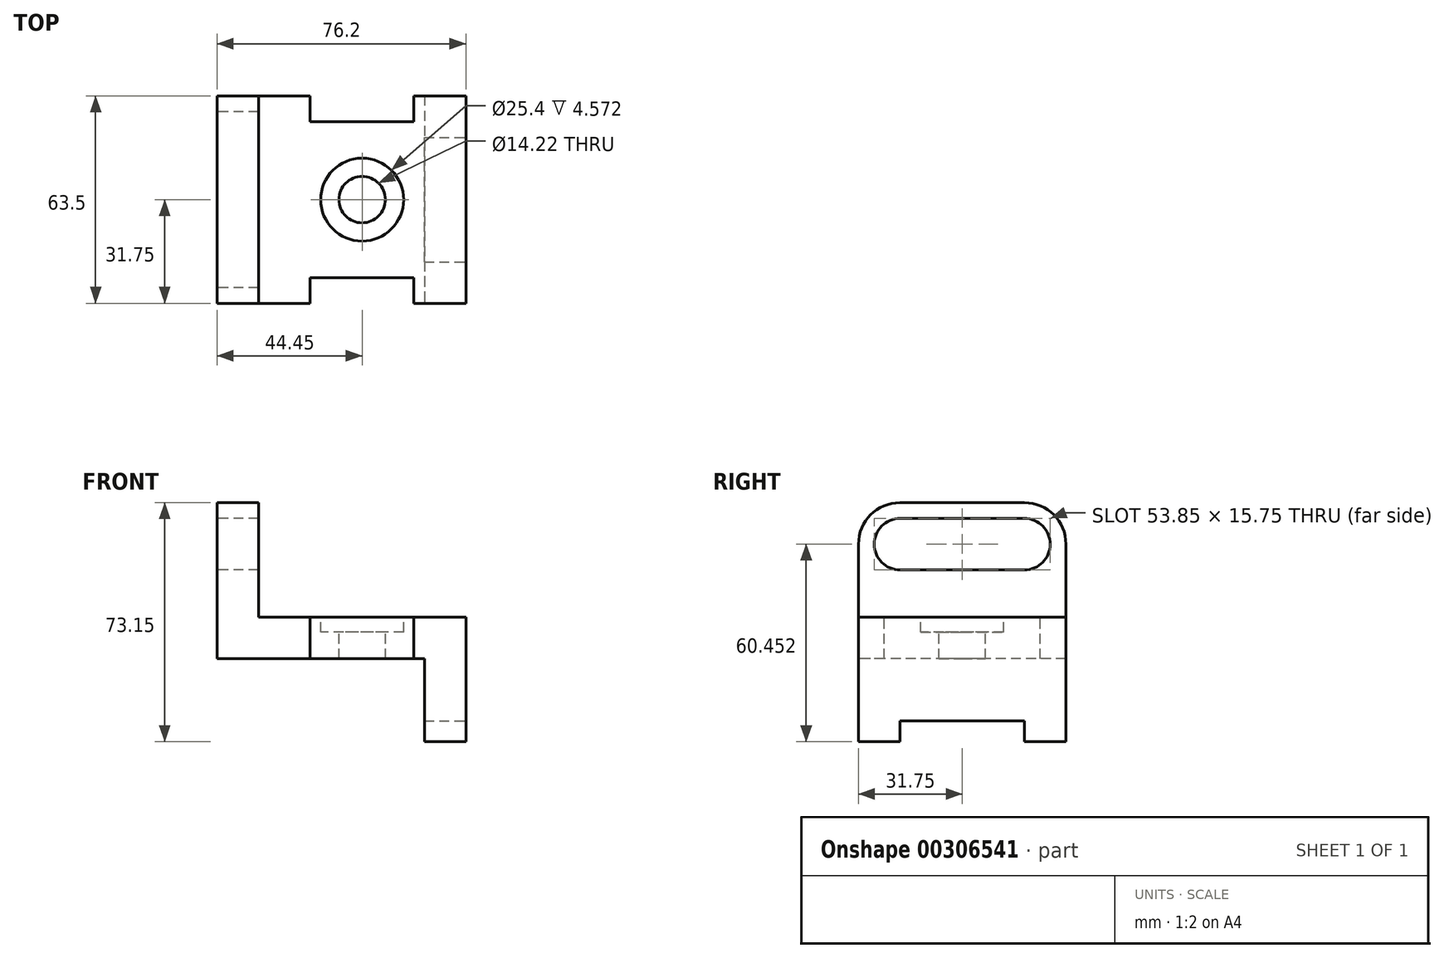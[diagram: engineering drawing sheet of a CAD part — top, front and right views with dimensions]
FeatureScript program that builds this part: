
annotation { "Feature Type Name" : "Feature", "Feature Type Description" : "" }
export const myFeature = defineFeature(function(context is Context, id is Id, definition is map)
    precondition{}
    {
        {
            var Q0;
            Q0=qCreatedBy(makeId("Front.planeOp"),FACE);
            var sketch = newSketch(context, id + "F0", { "sketchPlane" : qUnion([Q0])});
            skLineSegment(sketch, "E0", {"start": v(0, 0) * mm, "end": v(0, 38.1) * mm});
            skLineSegment(sketch, "E1", {"start": v(0, 38.1) * mm, "end": v(76.2, 38.1) * mm});
            skLineSegment(sketch, "E2", {"start": v(76.2, 38.1) * mm, "end": v(76.2, 0) * mm});
            skLineSegment(sketch, "E3", {"start": v(76.2, 0) * mm, "end": v(0, 0) * mm});
            skSolve(sketch);
        }
        {
            var Q0;
            Q0 = qSketchRegion(id + "F0", true);
            extrude(context, id + "F1", {"entities" : qUnion([Q0]), "depth" : 63.5 * mm});
        }
        {
            var Q0;
            Q0=makeQuery(id+"F1.opExtrude","CAP_FACE",FACE,{"disambiguationData":[OSD([sQuery(id+"F0.wireOp",EDGE,"E0"),sQuery(id+"F0.wireOp",EDGE,"E1"),sQuery(id+"F0.wireOp",EDGE,"E2"),sQuery(id+"F0.wireOp",EDGE,"E3")])],"isStart":false});
            var sketch = newSketch(context, id + "F2", { "sketchPlane" : qUnion([Q0])});
            skLineSegment(sketch, "E4", {"start": v(63.5, 0) * mm, "end": v(63.5, 25.4) * mm});
            skLineSegment(sketch, "E5", {"start": v(63.5, 25.4) * mm, "end": v(60.2, 25.4) * mm});
            skLineSegment(sketch, "E6", {"start": v(60.2, 25.4) * mm, "end": v(0, 25.4) * mm});
            skLineSegment(sketch, "E7", {"start": v(0, 25.4) * mm, "end": v(0, 0) * mm});
            skLineSegment(sketch, "E8", {"start": v(0, 0) * mm, "end": v(63.5, 0) * mm});
            skSolve(sketch);
        }
        {
            var Q0;
            Q0 = qSketchRegion(id + "F2", true);
            extrude(context, id + "F3", {"entities" : qUnion([Q0]), "operationType" : NewBodyOperationType.REMOVE, "endBound" : BoundingType.THROUGH_ALL, "oppositeDirection" : true, "depth" : 25.4 * mm});
        }
        {
            var Q0;
            Q0=makeQuery(id+"F1.opExtrude","CAP_FACE",FACE,{"disambiguationData":[OSD([sQuery(id+"F0.wireOp",EDGE,"E0"),sQuery(id+"F0.wireOp",EDGE,"E1"),sQuery(id+"F0.wireOp",EDGE,"E2"),sQuery(id+"F0.wireOp",EDGE,"E3")])],"isStart":false});
            var sketch = newSketch(context, id + "F4", { "sketchPlane" : qUnion([Q0])});
            skLineSegment(sketch, "E9", {"start": v(63.5, 25.4) * mm, "end": v(60.2, 25.4) * mm});
            skLineSegment(sketch, "E10", {"start": v(60.2, 25.4) * mm, "end": v(60.2, 38.1) * mm});
            skLineSegment(sketch, "E11", {"start": v(60.2, 38.1) * mm, "end": v(28.45, 38.1) * mm});
            skLineSegment(sketch, "E12", {"start": v(28.45, 38.1) * mm, "end": v(28.45, 25.4) * mm});
            skLineSegment(sketch, "E13", {"start": v(28.45, 25.4) * mm, "end": v(60.2, 25.4) * mm});
            skSolve(sketch);
        }
        {
            var Q0;
            Q0 = qSketchRegion(id + "F4", true);
            extrude(context, id + "F5", {"entities" : qUnion([Q0]), "operationType" : NewBodyOperationType.REMOVE, "oppositeDirection" : true, "depth" : 7.87 * mm});
        }
        {
            var Q0;
            Q0=makeQuery(id+"F1.opExtrude","SWEPT_FACE",FACE,{"disambiguationData":[OSD([sQuery(id+"F0.wireOp",EDGE,"E2")])]});
            var sketch = newSketch(context, id + "F6", { "sketchPlane" : qUnion([Q0])});
            skLineSegment(sketch, "E14", {"start": v(-50.8, 0) * mm, "end": v(-50.8, 6.35) * mm});
            skLineSegment(sketch, "E15", {"start": v(-50.8, 6.35) * mm, "end": v(-12.7, 6.35) * mm});
            skLineSegment(sketch, "E16", {"start": v(-12.7, 6.35) * mm, "end": v(-12.7, 0) * mm});
            skLineSegment(sketch, "E17", {"start": v(-12.7, 0) * mm, "end": v(-50.8, 0) * mm});
            skSolve(sketch);
        }
        {
            var Q0;
            Q0 = qSketchRegion(id + "F6", true);
            extrude(context, id + "F7", {"entities" : qUnion([Q0]), "operationType" : NewBodyOperationType.REMOVE, "endBound" : BoundingType.THROUGH_ALL, "oppositeDirection" : true, "depth" : 25.4 * mm});
        }
        {
            var Q0;
            Q0=qCreatedBy(makeId("Right.planeOp"),FACE);
            var sketch = newSketch(context, id + "F8", { "sketchPlane" : qUnion([Q0])});
            skLineSegment(sketch, "E18", {"start": v(0, 38.1) * mm, "end": v(0, 60.45) * mm});
            skLineSegment(sketch, "E19", {"start": v(-63.5, 38.1) * mm, "end": v(-63.5, 60.45) * mm});
            skLineSegment(sketch, "E20", {"start": v(-84.37, 60.45) * mm, "end": v(27.5, 60.45) * mm, "construction": true});
            skArc(sketch, "E21", {"start": v(-50.8, 68.33) * mm, "mid": v(-58.67, 60.45) * mm, "end": v(-50.8, 52.58) * mm});
            skArc(sketch, "E22", {"start": v(-12.7, 68.33) * mm, "mid": v(-4.83, 60.45) * mm, "end": v(-12.7, 52.58) * mm});
            skLineSegment(sketch, "E23", {"start": v(-50.8, 52.58) * mm, "end": v(-12.7, 52.58) * mm});
            skLineSegment(sketch, "E24", {"start": v(-12.7, 68.33) * mm, "end": v(-50.8, 68.33) * mm});
            skArc(sketch, "E25", {"start": v(-63.5, 60.45) * mm, "mid": v(-59.78, 69.43) * mm, "end": v(-50.8, 73.15) * mm});
            skArc(sketch, "E26", {"start": v(0, 60.45) * mm, "mid": v(-3.72, 69.43) * mm, "end": v(-12.7, 73.15) * mm});
            skLineSegment(sketch, "E27", {"start": v(-50.8, 73.15) * mm, "end": v(-12.7, 73.15) * mm});
            skLineSegment(sketch, "E28", {"start": v(-63.5, 38.1) * mm, "end": v(0, 38.1) * mm});
            skSolve(sketch);
        }
        {
            var Q0;
            Q0=makeQuery(id+"F8.imprint","IMPRINT",FACE,{"disambiguationData":[TD([[makeQuery(id+"F8.imprint","IMPRINT",EDGE,{"derivedFrom":sQuery(id+"F8.wireOp",EDGE,"E18")}),1.0]])]});
            extrude(context, id + "F9", {"entities" : qUnion([Q0]), "operationType" : NewBodyOperationType.ADD, "depth" : 12.7 * mm});
        }
        {
            var Q0;
            Q0=makeQuery(id+"F1.opExtrude","SWEPT_FACE",FACE,{"disambiguationData":[OSD([sQuery(id+"F0.wireOp",EDGE,"E1")])]});
            var sketch = newSketch(context, id + "F10", { "sketchPlane" : qUnion([Q0])});
            skCircle(sketch, "E29", {"center": v(44.45, -31.75) * mm, "radius": 12.7 * mm});
            skCircle(sketch, "E30", {"center": v(44.45, -31.75) * mm, "radius": 7.11 * mm});
            skSolve(sketch);
        }
        {
            var Q0;
            Q0=makeQuery(id+"F10.imprint","IMPRINT",FACE,{"disambiguationData":[TD([[makeQuery(id+"F10.imprint","IMPRINT",EDGE,{"derivedFrom":sQuery(id+"F10.wireOp",EDGE,"E29")}),1.0]])]});
            extrude(context, id + "F11", {"entities" : qUnion([Q0]), "operationType" : NewBodyOperationType.REMOVE, "oppositeDirection" : true, "depth" : 4.57 * mm});
        }
        {
            var Q0;
            Q0=makeQuery(id+"F11.boolean.opBoolean","SPLIT",FACE,{"disambiguationData":[TD([makeQuery(id+"F11.opExtrude","SWEPT_FACE",FACE,{"disambiguationData":[OSD([sQuery(id+"F10.wireOp",EDGE,"E30")])]})])],"derivedFrom":makeQuery(id+"F1.opExtrude","SWEPT_FACE",FACE,{"disambiguationData":[OSD([sQuery(id+"F0.wireOp",EDGE,"E1")])]})});
            extrude(context, id + "F12", {"entities" : qUnion([Q0]), "operationType" : NewBodyOperationType.REMOVE, "endBound" : BoundingType.THROUGH_ALL, "oppositeDirection" : true, "depth" : 25.4 * mm});
        }
        {
            var Q0;
            {var subQ1=sQuery(id+"F0.wireOp",EDGE,"E2");var subQ3=sQuery(id+"F0.wireOp",EDGE,"E1");Q0=makeQuery(id+"F11.boolean.opBoolean","SPLIT",FACE,{"disambiguationData":[TD([makeQuery(id+"F1.opExtrude","SWEPT_FACE",FACE,{"disambiguationData":[OSD([subQ1])]})])],"derivedFrom":makeQuery(id+"F1.opExtrude","SWEPT_FACE",FACE,{"disambiguationData":[OSD([subQ3])]})});}
            var sketch = newSketch(context, id + "F13", { "sketchPlane" : qUnion([Q0])});
            skLineSegment(sketch, "E31", {"start": v(28.45, 0) * mm, "end": v(60.2, 0) * mm});
            skLineSegment(sketch, "E32", {"start": v(60.2, 0) * mm, "end": v(60.2, -7.87) * mm});
            skLineSegment(sketch, "E33", {"start": v(60.2, -7.87) * mm, "end": v(28.45, -7.87) * mm});
            skLineSegment(sketch, "E34", {"start": v(28.45, -7.87) * mm, "end": v(28.45, 0) * mm});
            skSolve(sketch);
        }
        {
            var Q0;
            Q0 = qSketchRegion(id + "F13", true);
            extrude(context, id + "F14", {"entities" : qUnion([Q0]), "operationType" : NewBodyOperationType.REMOVE, "endBound" : BoundingType.THROUGH_ALL, "oppositeDirection" : true, "depth" : 25.4 * mm});
        }
    });
